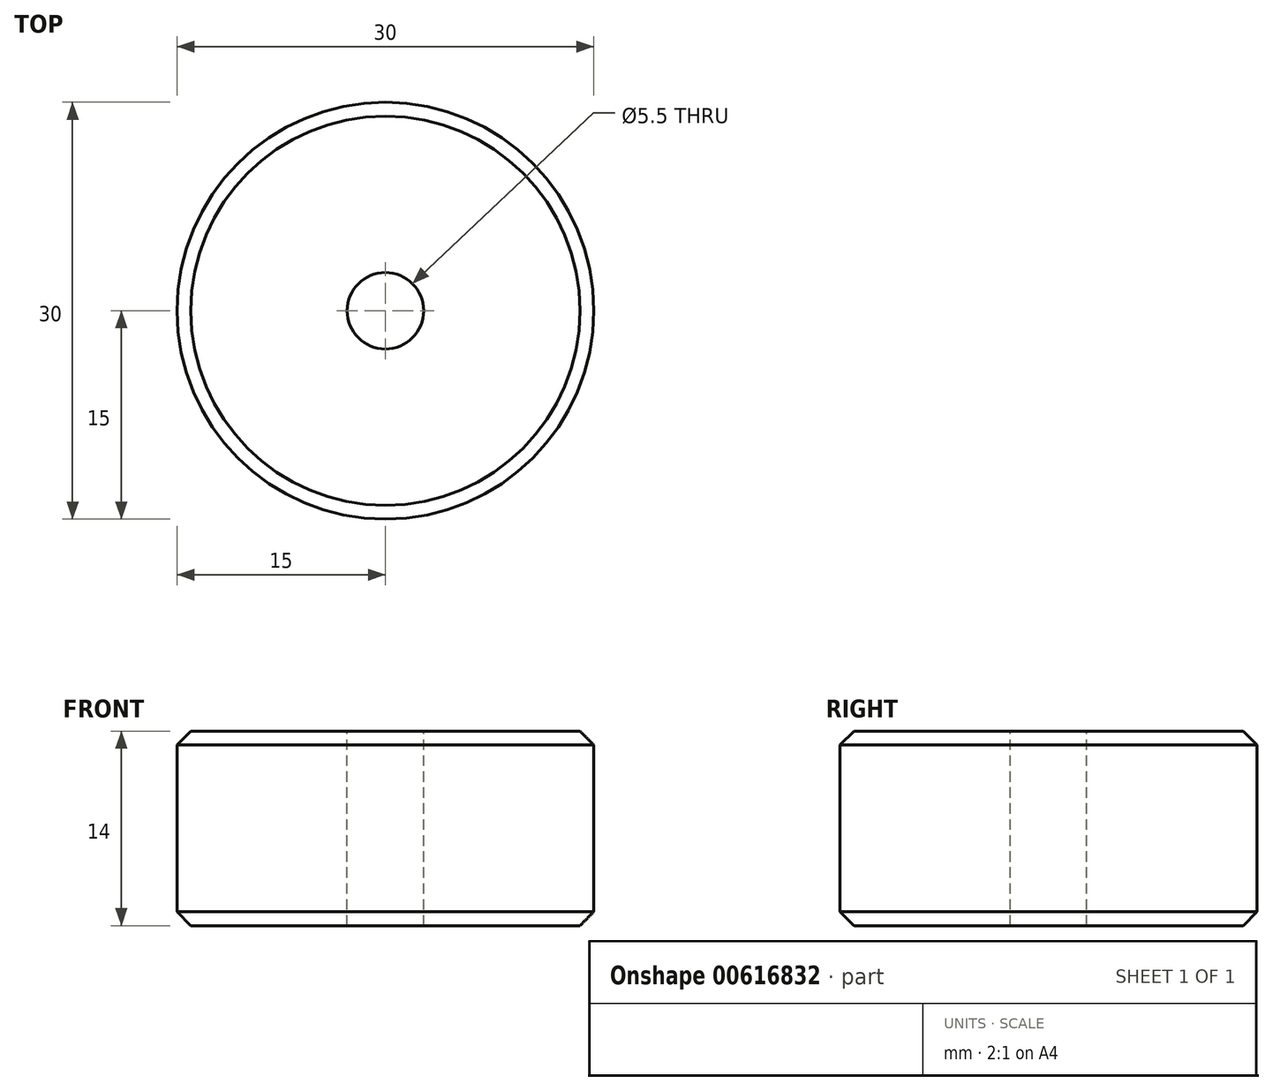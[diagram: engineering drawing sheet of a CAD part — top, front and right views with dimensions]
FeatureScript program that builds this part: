
annotation { "Feature Type Name" : "Feature", "Feature Type Description" : "" }
export const myFeature = defineFeature(function(context is Context, id is Id, definition is map)
    precondition{}
    {
        {
            var Q0;
            Q0=qCreatedBy(makeId("Front.planeOp"),FACE);
            var sketch = newSketch(context, id + "F0", { "sketchPlane" : qUnion([Q0])});
            skLineSegment(sketch, "E0.bottom", {"start": v(2.75, 14) * mm, "end": v(15, 14) * mm});
            skLineSegment(sketch, "E0.top", {"start": v(2.75, 0) * mm, "end": v(15, 0) * mm});
            skLineSegment(sketch, "E0.left", {"start": v(2.75, 14) * mm, "end": v(2.75, 0) * mm});
            skLineSegment(sketch, "E0.right", {"start": v(15, 14) * mm, "end": v(15, 0) * mm});
            skLineSegment(sketch, "E1", {"start": v(0, 42.73) * mm, "end": v(0, 0) * mm, "construction": true});
            skSolve(sketch);
        }
        {
            var Q0;
            Q0=makeQuery(id+"F0.imprint","IMPRINT",FACE,{"disambiguationData":[TD([[makeQuery(id+"F0.imprint","IMPRINT",EDGE,{"derivedFrom":sQuery(id+"F0.wireOp",EDGE,"E0.bottom")}),-1.0]])]});
            var Q1;
            Q1=sQuery(id+"F0.wireOp",EDGE,"E1");
            revolve(context, id + "F1", {"surfaceOperationType" : NewSurfaceOperationType.NEW, "entities" : qUnion([Q0]), "axis" : qUnion([Q1]), "revolveType" : RevolveType.FULL});
        }
        {
            var Q0;
            Q0=makeQuery(id+"F1.opRevolve","SWEPT_EDGE",EDGE,{"disambiguationData":[OSD([sQuery(id+"F0.wireOp",EDGE,"E0.bottom"),sQuery(id+"F0.wireOp",EDGE,"E0.right")])]});
            var Q1;
            Q1=makeQuery(id+"F1.opRevolve","SWEPT_EDGE",EDGE,{"disambiguationData":[OSD([sQuery(id+"F0.wireOp",EDGE,"E0.top"),sQuery(id+"F0.wireOp",EDGE,"E0.right")])]});
            chamfer(context, id + "F2", {"entities" : qUnion([Q0, Q1]), "width" : 1 * mm, "tangentPropagation" : true});
        }
    });
